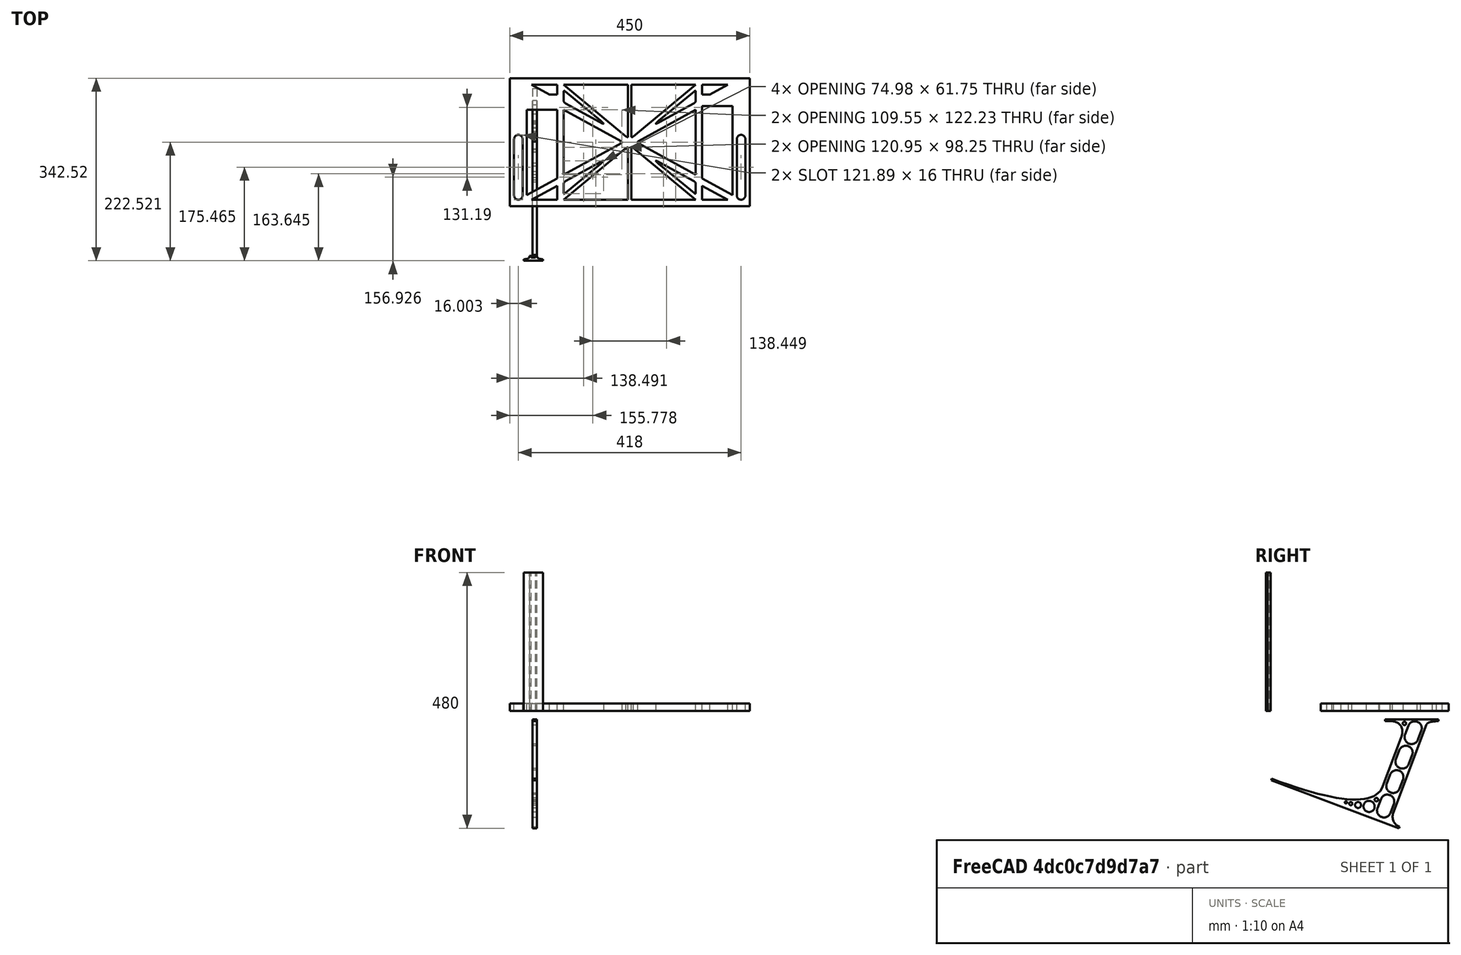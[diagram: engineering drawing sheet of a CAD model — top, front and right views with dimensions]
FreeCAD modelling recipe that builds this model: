
FCSTD DOCUMENT  (FreeCAD 0.19R0.19.2)
Label: laptopStand077
License: All rights reserved
LicenseURL: http://en.wikipedia.org/wiki/All_rights_reserved
objects: Sketcher::SketchObject×3, Part::Extrusion×3
note: 6 computed .brp shape members not serialized (recipe doc carries the construction recipe); baked Part::Feature solids carry a one-line shape summary decoded from their .brp

FEATURE [Sketcher::SketchObject] Sketch
  FullyConstrained = true
  sketch-geometry (172):
    g0: LineSegment StartX=-10.9272 StartY=-82.7794 StartZ=0 EndX=46.0728 EndY=-51.4823 EndZ=0
    g1: LineSegment StartX=366.073 StartY=-91.7794 StartZ=0 EndX=318.073 EndY=-65.424 EndZ=0
    g2: LineSegment StartX=-10.9272 StartY=77.3346 StartZ=0 EndX=-10.9272 EndY=-82.7794 EndZ=0
    g3: LineSegment StartX=375.073 StartY=-82.7794 StartZ=0 EndX=375.073 EndY=83.9235 EndZ=0
    g4: LineSegment StartX=-1.92719 StartY=-91.7794 StartZ=0 EndX=46.0728 EndY=-91.7794 EndZ=0
    g5: LineSegment StartX=318.073 StartY=124.221 StartZ=0 EndX=366.073 EndY=124.221 EndZ=0
    g6: LineSegment StartX=306.073 StartY=124.221 StartZ=0 EndX=189.124 EndY=27.0628 EndZ=0
    g7: LineSegment StartX=58.0728 StartY=-91.7794 StartZ=0 EndX=175.022 EndY=5.37834 EndZ=0
    g8: LineSegment StartX=175.022 StartY=27.0628 StartZ=0 EndX=58.0728 EndY=124.221 EndZ=0
    g9: LineSegment StartX=189.124 StartY=5.37834 StartZ=0 EndX=306.073 EndY=-91.7794 EndZ=0
    g10: LineSegment StartX=306.073 StartY=77.3346 StartZ=0 EndX=306.073 EndY=-44.8935 EndZ=0
    g11: LineSegment StartX=318.073 StartY=83.9235 StartZ=0 EndX=318.073 EndY=-51.4823 EndZ=0
    g12: LineSegment StartX=318.073 StartY=-51.4823 StartZ=0 EndX=375.073 EndY=-82.7794 EndZ=0
    g13: LineSegment StartX=318.073 StartY=-65.424 StartZ=0 EndX=318.073 EndY=-91.7794 EndZ=0
    g14: LineSegment StartX=318.073 StartY=-91.7794 StartZ=0 EndX=366.073 EndY=-91.7794 EndZ=0
    g15: LineSegment StartX=58.0728 StartY=-44.8935 StartZ=0 EndX=58.0728 EndY=77.3346 EndZ=0
    g16: LineSegment StartX=46.0728 StartY=-65.424 StartZ=0 EndX=-1.92719 EndY=-91.7794 EndZ=0
    g17: LineSegment StartX=46.0728 StartY=-65.424 StartZ=0 EndX=46.0728 EndY=-91.7794 EndZ=0
    g18: LineSegment StartX=46.0728 StartY=77.3346 StartZ=0 EndX=46.0728 EndY=-51.4823 EndZ=0
    g19: LineSegment StartX=-42.9272 StartY=136.221 StartZ=0 EndX=-42.9272 EndY=-103.779 EndZ=0
    g20: LineSegment StartX=407.073 StartY=136.221 StartZ=0 EndX=407.073 EndY=-103.779 EndZ=0
    g21: LineSegment StartX=179.022 StartY=27.0628 StartZ=0 EndX=179.022 EndY=124.221 EndZ=0
    g22: LineSegment StartX=185.124 StartY=27.0628 StartZ=0 EndX=185.124 EndY=124.221 EndZ=0
    g23: ArcOfCircle CenterX=-26.9272 CenterY=22.1087 CenterZ=0 NormalX=0 NormalY=0 NormalZ=1 AngleXU=0 Radius=8 StartAngle=1e-16 EndAngle=3.14159
    g24: ArcOfCircle CenterX=-26.9272 CenterY=-83.7794 CenterZ=0 NormalX=0 NormalY=0 NormalZ=1 AngleXU=0 Radius=8 StartAngle=3.14159 EndAngle=6.28319
    g25: LineSegment StartX=-34.9272 StartY=22.1087 StartZ=0 EndX=-34.9272 EndY=-83.7794 EndZ=0
    g26: LineSegment StartX=-18.9272 StartY=22.1087 StartZ=0 EndX=-18.9272 EndY=-83.7794 EndZ=0
    g27: LineSegment StartX=185.124 StartY=-91.7794 StartZ=0 EndX=306.073 EndY=-91.7794 EndZ=0
    g28: LineSegment StartX=179.022 StartY=-91.7794 StartZ=0 EndX=58.0728 EndY=-91.7794 EndZ=0
    g29: LineSegment StartX=306.073 StartY=124.221 StartZ=0 EndX=185.124 EndY=124.221 EndZ=0
    g30: LineSegment StartX=179.022 StartY=124.221 StartZ=0 EndX=58.0728 EndY=124.221 EndZ=0
    g31: ArcOfCircle CenterX=391.073 CenterY=22.1087 CenterZ=0 NormalX=0 NormalY=0 NormalZ=1 AngleXU=0 Radius=8 StartAngle=-4.4e-15 EndAngle=3.14159
    g32: LineSegment StartX=399.073 StartY=22.1087 StartZ=0 EndX=399.073 EndY=-83.7794 EndZ=0
    g33: LineSegment StartX=383.073 StartY=22.1087 StartZ=0 EndX=383.073 EndY=-83.7794 EndZ=0
    g34: ArcOfCircle CenterX=391.073 CenterY=-83.7794 CenterZ=0 NormalX=0 NormalY=0 NormalZ=1 AngleXU=0 Radius=8 StartAngle=3.14159 EndAngle=6.28319
    g35: Circle CenterX=175.022 CenterY=27.0628 CenterZ=0 NormalX=0 NormalY=0 NormalZ=1 AngleXU=0 Radius=1
    g36: Circle CenterX=179.022 CenterY=24.8665 CenterZ=0 NormalX=0 NormalY=0 NormalZ=1 AngleXU=0 Radius=1
    g37: Circle CenterX=179.022 CenterY=27.0628 CenterZ=0 NormalX=0 NormalY=0 NormalZ=1 AngleXU=0 Radius=1
    g38: BSplineCurve PolesCount=3 KnotsCount=2 Degree=2 IsPeriodic=0
    g39: GeomPoint X=175.022 Y=27.0628 Z=0
    g40: GeomPoint X=179.022 Y=27.0628 Z=0
    g41: Circle CenterX=189.124 CenterY=27.0628 CenterZ=0 NormalX=0 NormalY=0 NormalZ=1 AngleXU=0 Radius=1
    g42: Circle CenterX=185.124 CenterY=24.8665 CenterZ=0 NormalX=0 NormalY=0 NormalZ=1 AngleXU=0 Radius=1
    g43: Circle CenterX=185.124 CenterY=27.0628 CenterZ=0 NormalX=0 NormalY=0 NormalZ=1 AngleXU=0 Radius=1
    g44: BSplineCurve PolesCount=3 KnotsCount=2 Degree=2 IsPeriodic=0
    g45: GeomPoint X=189.124 Y=27.0628 Z=0
    g46: GeomPoint X=185.124 Y=27.0628 Z=0
    g47: Circle CenterX=175.022 CenterY=5.37834 CenterZ=0 NormalX=0 NormalY=0 NormalZ=1 AngleXU=0 Radius=1
    g48: Circle CenterX=179.022 CenterY=7.57463 CenterZ=0 NormalX=0 NormalY=0 NormalZ=1 AngleXU=0 Radius=1
    g49: Circle CenterX=179.022 CenterY=5.34704 CenterZ=0 NormalX=0 NormalY=0 NormalZ=1 AngleXU=0 Radius=1
    g50: BSplineCurve PolesCount=3 KnotsCount=2 Degree=2 IsPeriodic=0
    g51: GeomPoint X=175.022 Y=5.37834 Z=0
    g52: GeomPoint X=179.022 Y=5.34704 Z=0
    g53: Circle CenterX=189.124 CenterY=5.37834 CenterZ=0 NormalX=0 NormalY=0 NormalZ=1 AngleXU=0 Radius=1
    g54: Circle CenterX=185.124 CenterY=7.57463 CenterZ=0 NormalX=0 NormalY=0 NormalZ=1 AngleXU=0 Radius=1
    g55: Circle CenterX=185.124 CenterY=5.34704 CenterZ=0 NormalX=0 NormalY=0 NormalZ=1 AngleXU=0 Radius=1
    g56: BSplineCurve PolesCount=3 KnotsCount=2 Degree=2 IsPeriodic=0
    g57: GeomPoint X=189.124 Y=5.37834 Z=0
    g58: GeomPoint X=185.124 Y=5.34704 Z=0
    g59: LineSegment StartX=179.022 StartY=5.34704 StartZ=0 EndX=179.022 EndY=-91.7794 EndZ=0
    g60: LineSegment StartX=185.124 StartY=-91.7794 StartZ=0 EndX=185.124 EndY=5.34704 EndZ=0
    g61: Circle CenterX=165.871 CenterY=18.1458 CenterZ=0 NormalX=0 NormalY=0 NormalZ=1 AngleXU=0 Radius=1
    g62: Circle CenterX=169.377 CenterY=16.2206 CenterZ=0 NormalX=0 NormalY=0 NormalZ=1 AngleXU=0 Radius=1
    g63: Circle CenterX=165.871 CenterY=14.2954 CenterZ=0 NormalX=0 NormalY=0 NormalZ=1 AngleXU=0 Radius=1
    g64: BSplineCurve PolesCount=3 KnotsCount=2 Degree=2 IsPeriodic=0
    g65: GeomPoint X=165.871 Y=18.1458 Z=0
    g66: GeomPoint X=165.871 Y=14.2954 Z=0
    g67: Circle CenterX=198.275 CenterY=18.1458 CenterZ=0 NormalX=0 NormalY=0 NormalZ=1 AngleXU=0 Radius=1
    g68: Circle CenterX=194.768 CenterY=16.2206 CenterZ=0 NormalX=0 NormalY=0 NormalZ=1 AngleXU=0 Radius=1
    g69: Circle CenterX=198.275 CenterY=14.2954 CenterZ=0 NormalX=0 NormalY=0 NormalZ=1 AngleXU=0 Radius=1
    g70: BSplineCurve PolesCount=3 KnotsCount=2 Degree=2 IsPeriodic=0
    g71: GeomPoint X=198.275 Y=18.1458 Z=0
    g72: GeomPoint X=198.275 Y=14.2954 Z=0
    g73: LineSegment StartX=165.871 StartY=18.1458 StartZ=0 EndX=58.0728 EndY=77.3346 EndZ=0
    g74: LineSegment StartX=58.0728 StartY=-44.8935 StartZ=0 EndX=165.871 EndY=14.2954 EndZ=0
    g75: LineSegment StartX=198.275 StartY=18.1458 StartZ=0 EndX=306.073 EndY=77.3346 EndZ=0
    g76: LineSegment StartX=198.275 StartY=14.2954 StartZ=0 EndX=306.073 EndY=-44.8935 EndZ=0
    g77: LineSegment StartX=407.073 StartY=-103.779 StartZ=0 EndX=-42.9272 EndY=-103.779 EndZ=0
    g78: LineSegment StartX=407.073 StartY=136.221 StartZ=0 EndX=-42.9272 EndY=136.221 EndZ=0
    g79: LineSegment StartX=46.0728 StartY=77.3346 StartZ=0 EndX=-10.9272 EndY=77.3346 EndZ=0
    g80: LineSegment StartX=46.0728 StartY=105.865 StartZ=0 EndX=31.5028 EndY=105.865 EndZ=0
    g81: LineSegment StartX=46.0728 StartY=124.221 StartZ=0 EndX=46.0728 EndY=105.865 EndZ=0
    g82: LineSegment StartX=-1.92719 StartY=124.221 StartZ=0 EndX=31.5028 EndY=105.865 EndZ=0
    g83: LineSegment StartX=46.0728 StartY=124.221 StartZ=0 EndX=-1.92719 EndY=124.221 EndZ=0
    g84: LineSegment StartX=318.073 StartY=83.9235 StartZ=0 EndX=375.073 EndY=83.9235 EndZ=0
    g85: LineSegment StartX=318.073 StartY=105.865 StartZ=0 EndX=332.643 EndY=105.865 EndZ=0
    g86: LineSegment StartX=332.643 StartY=105.865 StartZ=0 EndX=366.073 EndY=124.221 EndZ=0
    g87: LineSegment StartX=318.073 StartY=124.221 StartZ=0 EndX=318.073 EndY=105.865 EndZ=0
    g88: Circle CenterX=125.607 CenterY=54.1951 CenterZ=0 NormalX=0 NormalY=0 NormalZ=1 AngleXU=0 Radius=1
    g89: Circle CenterX=139.632 CenterY=46.4944 CenterZ=0 NormalX=0 NormalY=0 NormalZ=1 AngleXU=0 Radius=1
    g90: Circle CenterX=127.326 CenterY=56.7187 CenterZ=0 NormalX=0 NormalY=0 NormalZ=1 AngleXU=0 Radius=1
    g91: BSplineCurve PolesCount=3 KnotsCount=2 Degree=2 IsPeriodic=0
    g92: GeomPoint X=125.607 Y=54.1951 Z=0
    g93: GeomPoint X=127.326 Y=56.7187 Z=0
    g94: Circle CenterX=236.821 CenterY=56.7187 CenterZ=0 NormalX=0 NormalY=0 NormalZ=1 AngleXU=0 Radius=1
    g95: Circle CenterX=224.513 CenterY=46.4944 CenterZ=0 NormalX=0 NormalY=0 NormalZ=1 AngleXU=0 Radius=1
    g96: Circle CenterX=238.538 CenterY=54.1951 CenterZ=0 NormalX=0 NormalY=0 NormalZ=1 AngleXU=0 Radius=1
    g97: BSplineCurve PolesCount=3 KnotsCount=2 Degree=2 IsPeriodic=0
    g98: GeomPoint X=236.821 Y=56.7187 Z=0
    g99: GeomPoint X=238.538 Y=54.1951 Z=0
    g100: Circle CenterX=238.538 CenterY=-21.7539 CenterZ=0 NormalX=0 NormalY=0 NormalZ=1 AngleXU=0 Radius=1
    g101: Circle CenterX=224.513 CenterY=-14.0532 CenterZ=0 NormalX=0 NormalY=0 NormalZ=1 AngleXU=0 Radius=1
    g102: Circle CenterX=236.821 CenterY=-24.2775 CenterZ=0 NormalX=0 NormalY=0 NormalZ=1 AngleXU=0 Radius=1
    g103: BSplineCurve PolesCount=3 KnotsCount=2 Degree=2 IsPeriodic=0
    g104: GeomPoint X=238.538 Y=-21.7539 Z=0
    g105: GeomPoint X=236.821 Y=-24.2775 Z=0
    g106: Circle CenterX=125.607 CenterY=-21.7539 CenterZ=0 NormalX=0 NormalY=0 NormalZ=1 AngleXU=0 Radius=1
    g107: Circle CenterX=139.632 CenterY=-14.0532 CenterZ=0 NormalX=0 NormalY=0 NormalZ=1 AngleXU=0 Radius=1
    g108: Circle CenterX=127.325 CenterY=-24.2775 CenterZ=0 NormalX=0 NormalY=0 NormalZ=1 AngleXU=0 Radius=1
    g109: BSplineCurve PolesCount=3 KnotsCount=2 Degree=2 IsPeriodic=0
    g110: GeomPoint X=125.607 Y=-21.7539 Z=0
    g111: GeomPoint X=127.325 Y=-24.2775 Z=0
    g112: Circle CenterX=302.996 CenterY=111.695 CenterZ=0 NormalX=0 NormalY=0 NormalZ=1 AngleXU=0 Radius=1
    g113: Circle CenterX=306.073 CenterY=114.251 CenterZ=0 NormalX=0 NormalY=0 NormalZ=1 AngleXU=0 Radius=1
    g114: Circle CenterX=306.073 CenterY=110.251 CenterZ=0 NormalX=0 NormalY=0 NormalZ=1 AngleXU=0 Radius=1
    g115: BSplineCurve PolesCount=3 KnotsCount=2 Degree=2 IsPeriodic=0
    g116: GeomPoint X=302.996 Y=111.695 Z=0
    g117: GeomPoint X=306.073 Y=110.251 Z=0
    g118: Circle CenterX=306.073 CenterY=95.2763 CenterZ=0 NormalX=0 NormalY=0 NormalZ=1 AngleXU=0 Radius=1
    g119: Circle CenterX=306.073 CenterY=91.2763 CenterZ=0 NormalX=0 NormalY=0 NormalZ=1 AngleXU=0 Radius=1
    g120: Circle CenterX=302.567 CenterY=89.3511 CenterZ=0 NormalX=0 NormalY=0 NormalZ=1 AngleXU=0 Radius=1
    g121: BSplineCurve PolesCount=3 KnotsCount=2 Degree=2 IsPeriodic=0
    g122: GeomPoint X=306.073 Y=95.2763 Z=0
    g123: GeomPoint X=302.567 Y=89.3511 Z=0
    g124: LineSegment StartX=306.073 StartY=110.251 StartZ=0 EndX=306.073 EndY=95.2763 EndZ=0
    g125: LineSegment StartX=302.996 StartY=111.695 StartZ=0 EndX=236.821 EndY=56.7187 EndZ=0
    g126: LineSegment StartX=238.538 StartY=54.1951 StartZ=0 EndX=302.567 EndY=89.3511 EndZ=0
    g127: Circle CenterX=61.1496 CenterY=111.695 CenterZ=0 NormalX=0 NormalY=0 NormalZ=1 AngleXU=0 Radius=1
    g128: Circle CenterX=58.0728 CenterY=114.251 CenterZ=0 NormalX=0 NormalY=0 NormalZ=1 AngleXU=0 Radius=1
    g129: Circle CenterX=58.0728 CenterY=110.251 CenterZ=0 NormalX=0 NormalY=0 NormalZ=1 AngleXU=0 Radius=1
    g130: BSplineCurve PolesCount=3 KnotsCount=2 Degree=2 IsPeriodic=0
    g131: GeomPoint X=61.1496 Y=111.695 Z=0
    g132: GeomPoint X=58.0728 Y=110.251 Z=0
    g133: Circle CenterX=61.5791 CenterY=89.3511 CenterZ=0 NormalX=0 NormalY=0 NormalZ=1 AngleXU=0 Radius=1
    g134: Circle CenterX=58.0728 CenterY=91.2763 CenterZ=0 NormalX=0 NormalY=0 NormalZ=1 AngleXU=0 Radius=1
    g135: Circle CenterX=58.0728 CenterY=95.2763 CenterZ=0 NormalX=0 NormalY=0 NormalZ=1 AngleXU=0 Radius=1
    g136: BSplineCurve PolesCount=3 KnotsCount=2 Degree=2 IsPeriodic=0
    g137: GeomPoint X=61.5791 Y=89.3511 Z=0
    g138: GeomPoint X=58.0728 Y=95.2763 Z=0
    g139: LineSegment StartX=58.0728 StartY=110.251 StartZ=0 EndX=58.0728 EndY=95.2763 EndZ=0
    g140: LineSegment StartX=61.1496 StartY=111.695 StartZ=0 EndX=127.326 EndY=56.7187 EndZ=0
    g141: LineSegment StartX=125.607 StartY=54.1951 StartZ=0 EndX=61.5791 EndY=89.3511 EndZ=0
    g142: Circle CenterX=61.5791 CenterY=-56.9099 CenterZ=0 NormalX=0 NormalY=0 NormalZ=1 AngleXU=0 Radius=1
    g143: Circle CenterX=58.0728 CenterY=-58.8351 CenterZ=0 NormalX=0 NormalY=0 NormalZ=1 AngleXU=0 Radius=1
    g144: Circle CenterX=58.0728 CenterY=-62.8351 CenterZ=0 NormalX=0 NormalY=0 NormalZ=1 AngleXU=0 Radius=1
    g145: BSplineCurve PolesCount=3 KnotsCount=2 Degree=2 IsPeriodic=0
    g146: GeomPoint X=61.5791 Y=-56.9099 Z=0
    g147: GeomPoint X=58.0728 Y=-62.8351 Z=0
    g148: Circle CenterX=58.0728 CenterY=-77.8102 CenterZ=0 NormalX=0 NormalY=0 NormalZ=1 AngleXU=0 Radius=1
    g149: Circle CenterX=58.0728 CenterY=-81.8102 CenterZ=0 NormalX=0 NormalY=0 NormalZ=1 AngleXU=0 Radius=1
    g150: Circle CenterX=61.1496 CenterY=-79.2541 CenterZ=0 NormalX=0 NormalY=0 NormalZ=1 AngleXU=0 Radius=1
    g151: BSplineCurve PolesCount=3 KnotsCount=2 Degree=2 IsPeriodic=0
    g152: GeomPoint X=58.0728 Y=-77.8102 Z=0
    g153: GeomPoint X=61.1496 Y=-79.2541 Z=0
    g154: LineSegment StartX=58.0728 StartY=-62.8351 StartZ=0 EndX=58.0728 EndY=-77.8102 EndZ=0
    g155: LineSegment StartX=61.1496 StartY=-79.2541 StartZ=0 EndX=127.325 EndY=-24.2775 EndZ=0
    g156: LineSegment StartX=125.607 StartY=-21.7539 StartZ=0 EndX=61.5791 EndY=-56.9099 EndZ=0
    g157: Circle CenterX=302.567 CenterY=-56.9099 CenterZ=0 NormalX=0 NormalY=0 NormalZ=1 AngleXU=0 Radius=1
    g158: Circle CenterX=306.073 CenterY=-58.8351 CenterZ=0 NormalX=0 NormalY=0 NormalZ=1 AngleXU=0 Radius=1
    g159: Circle CenterX=306.073 CenterY=-62.8351 CenterZ=0 NormalX=0 NormalY=0 NormalZ=1 AngleXU=0 Radius=1
    g160: BSplineCurve PolesCount=3 KnotsCount=2 Degree=2 IsPeriodic=0
    g161: GeomPoint X=302.567 Y=-56.9099 Z=0
    g162: GeomPoint X=306.073 Y=-62.8351 Z=0
    g163: Circle CenterX=302.996 CenterY=-79.2541 CenterZ=0 NormalX=0 NormalY=0 NormalZ=1 AngleXU=0 Radius=1
    g164: Circle CenterX=306.073 CenterY=-81.8102 CenterZ=0 NormalX=0 NormalY=0 NormalZ=1 AngleXU=0 Radius=1
    g165: Circle CenterX=306.073 CenterY=-77.8102 CenterZ=0 NormalX=0 NormalY=0 NormalZ=1 AngleXU=0 Radius=1
    g166: BSplineCurve PolesCount=3 KnotsCount=2 Degree=2 IsPeriodic=0
    g167: GeomPoint X=302.996 Y=-79.2541 Z=0
    g168: GeomPoint X=306.073 Y=-77.8102 Z=0
    g169: LineSegment StartX=306.073 StartY=-62.8351 StartZ=0 EndX=306.073 EndY=-77.8102 EndZ=0
    g170: LineSegment StartX=302.996 StartY=-79.2541 StartZ=0 EndX=236.821 EndY=-24.2775 EndZ=0
    g171: LineSegment StartX=238.538 StartY=-21.7539 StartZ=0 EndX=302.567 EndY=-56.9099 EndZ=0
  constraints (300):
    c: Horizontal(g4)
    c: Horizontal(g5)
    c: Coincident(g11,g12)
    c: Coincident(g13,g1)
    c: Tangent(g11,g13)
    c: Coincident(g17,g16)
    c: Coincident(g0,g18)
    c: Block(g8)
    c: Block(g6)
    c: Block(g12)
    c: Block(g3)
    c: Block(g1)
    c: Block(g13)
    c: Block(g9)
    c: Block(g7)
    c: Block(g17)
    c: Block(g16)
    c: Block(g0)
    c: Block(g2)
    c: Block(g10)
    c: Block(g5)
    c: Block(g14)
    c: Block(g4)
    c: Vertical(g19)
    c: Vertical(g20)
    c: Block(g20)
    c: Block(g19)
    c: Vertical(g21)
    c: Vertical(g22)
    c: Block(g21)
    c: Block(g22)
    c: Tangent(g23,g26) = 1.5708
    c: Tangent(g23,g25) = -1.5708
    c: Tangent(g25,g24) = -1.5708
    c: Tangent(g26,g24) = 1.5708
    c: Vertical(g25)
    c: Equal(g23,g24)
    c: Block(g26)
    c: Block(g25)
    c: Coincident(g27,g9)
    c: Horizontal(g27)
    c: Coincident(g28,g7)
    c: Horizontal(g28)
    c: Coincident(g29,g6)
    c: Coincident(g29,g22)
    c: Horizontal(g29)
    c: Coincident(g30,g21)
    c: Coincident(g30,g8)
    c: Horizontal(g30)
    c: Tangent(g31,g32) = 1.5708
    c: Tangent(g32,g34) = 1.5708
    c: Equal(g31,g34)
    c: Coincident(g33,g31)
    c: Coincident(g33,g34)
    c: Block(g32)
    c: Block(g33)
    c: Coincident(g38,g8)
    c: Weight(g35) = 1
    c: Equal(g35,g36)
    c: Equal(g35,g37)
    c: Coincident(g38,g21)
    c: InternalAlignment(g35,g38)
    c: InternalAlignment(g36,g38)
    c: InternalAlignment(g37,g38)
    c: InternalAlignment(g39,g38)
    c: InternalAlignment(g40,g38)
    c: Coincident(g44,g6)
    c: Weight(g41) = 1
    c: Equal(g41,g42)
    c: Equal(g41,g43)
    c: Coincident(g44,g22)
    c: InternalAlignment(g41,g44)
    c: InternalAlignment(g42,g44)
    c: InternalAlignment(g43,g44)
    c: InternalAlignment(g45,g44)
    c: InternalAlignment(g46,g44)
    c: Block(g44)
    c: Block(g38)
    c: Coincident(g50,g7)
    c: Weight(g47) = 1
    c: Equal(g47,g48)
    c: Equal(g47,g49)
    c: InternalAlignment(g47,g50)
    c: InternalAlignment(g48,g50)
    c: InternalAlignment(g49,g50)
    c: InternalAlignment(g51,g50)
    c: InternalAlignment(g52,g50)
    c: Weight(g53) = 1
    c: Equal(g53,g54)
    c: Equal(g53,g55)
    c: InternalAlignment(g53,g56)
    c: InternalAlignment(g54,g56)
    c: InternalAlignment(g55,g56)
    c: InternalAlignment(g57,g56)
    c: InternalAlignment(g58,g56)
    c: Block(g56)
    c: Block(g50)
    c: Coincident(g59,g50)
    c: Coincident(g59,g28)
    c: Vertical(g59)
    c: Coincident(g60,g27)
    c: Coincident(g60,g56)
    c: Vertical(g60)
    c: Weight(g61) = 1
    c: Equal(g61,g62)
    c: Equal(g61,g63)
    c: InternalAlignment(g61,g64)
    c: InternalAlignment(g62,g64)
    c: InternalAlignment(g63,g64)
    c: InternalAlignment(g65,g64)
    c: InternalAlignment(g66,g64)
    c: Weight(g67) = 1
    c: Equal(g67,g68)
    c: Equal(g67,g69)
    c: InternalAlignment(g67,g70)
    c: InternalAlignment(g68,g70)
    c: InternalAlignment(g69,g70)
    c: InternalAlignment(g71,g70)
    c: InternalAlignment(g72,g70)
    c: Block(g64)
    c: Block(g70)
    c: Coincident(g73,g64)
    c: Coincident(g73,g15)
    c: Coincident(g74,g15)
    c: Coincident(g74,g64)
    c: Coincident(g75,g70)
    c: Coincident(g75,g10)
    c: Coincident(g76,g70)
    c: Coincident(g76,g10)
    c: Block(g15)
    c: Coincident(g77,g20)
    c: Coincident(g77,g19)
    c: Horizontal(g77)
    c: Distance(g77) = 450
    c: Coincident(g78,g20)
    c: Coincident(g78,g19)
    c: Horizontal(g78)
    c: Horizontal(g79)
    c: Coincident(g18,g79)
    c: Horizontal(g80)
    c: Vertical(g81)
    c: Block(g81)
    c: Block(g80)
    c: Block(g79)
    c: Distance(g81) = 18.3554
    c: Coincident(g83,g81)
    c: Coincident(g83,g82)
    c: Horizontal(g83)
    c: Block(g83)
    c: Block(g82)
    c: Coincident(g80,g82)
    c: Coincident(g2,g79)
    c: Coincident(g84,g11)
    c: Horizontal(g84)
    c: Horizontal(g85)
    c: Block(g84)
    c: Coincident(g86,g5)
    c: Coincident(g87,g5)
    c: Coincident(g87,g85)
    c: Vertical(g87)
    c: Block(g87)
    c: Coincident(g85,g86)
    c: Block(g86)
    c: Coincident(g3,g84)
    c: Weight(g88) = 1
    c: Equal(g88,g89)
    c: Equal(g88,g90)
    c: InternalAlignment(g88,g91)
    c: InternalAlignment(g89,g91)
    c: InternalAlignment(g90,g91)
    c: InternalAlignment(g92,g91)
    c: InternalAlignment(g93,g91)
    c: Block(g91)
    c: Weight(g94) = 1
    c: Equal(g94,g95)
    c: Equal(g94,g96)
    c: InternalAlignment(g94,g97)
    c: InternalAlignment(g95,g97)
    c: InternalAlignment(g96,g97)
    c: InternalAlignment(g98,g97)
    c: InternalAlignment(g99,g97)
    c: Block(g97)
    c: Weight(g100) = 1
    c: Equal(g100,g101)
    c: Equal(g100,g102)
    c: InternalAlignment(g100,g103)
    c: InternalAlignment(g101,g103)
    c: InternalAlignment(g102,g103)
    c: InternalAlignment(g104,g103)
    c: InternalAlignment(g105,g103)
    c: Block(g103)
    c: Weight(g106) = 1
    c: Equal(g106,g107)
    c: Equal(g106,g108)
    c: InternalAlignment(g106,g109)
    c: InternalAlignment(g107,g109)
    c: InternalAlignment(g108,g109)
    c: InternalAlignment(g110,g109)
    c: InternalAlignment(g111,g109)
    c: Block(g109)
    c: Weight(g112) = 1
    c: Equal(g112,g113)
    c: Equal(g112,g114)
    c: InternalAlignment(g112,g115)
    c: InternalAlignment(g113,g115)
    c: InternalAlignment(g114,g115)
    c: InternalAlignment(g116,g115)
    c: InternalAlignment(g117,g115)
    c: Weight(g118) = 1
    c: Equal(g118,g119)
    c: Equal(g118,g120)
    c: InternalAlignment(g118,g121)
    c: InternalAlignment(g119,g121)
    c: InternalAlignment(g120,g121)
    c: InternalAlignment(g122,g121)
    c: InternalAlignment(g123,g121)
    c: Block(g115)
    c: Block(g121)
    c: Coincident(g124,g115)
    c: Coincident(g124,g121)
    c: Vertical(g124)
    c: Coincident(g125,g115)
    c: Coincident(g125,g97)
    c: Coincident(g126,g97)
    c: Coincident(g126,g121)
    c: Weight(g127) = 1
    c: Equal(g127,g128)
    c: Equal(g127,g129)
    c: InternalAlignment(g127,g130)
    c: InternalAlignment(g128,g130)
    c: InternalAlignment(g129,g130)
    c: InternalAlignment(g131,g130)
    c: InternalAlignment(g132,g130)
    c: Weight(g133) = 1
    c: Equal(g133,g134)
    c: Equal(g133,g135)
    c: InternalAlignment(g133,g136)
    c: InternalAlignment(g134,g136)
    c: InternalAlignment(g135,g136)
    c: InternalAlignment(g137,g136)
    c: InternalAlignment(g138,g136)
    c: Block(g130)
    c: Block(g136)
    c: Coincident(g139,g130)
    c: Coincident(g139,g136)
    c: Vertical(g139)
    c: Coincident(g140,g130)
    c: Coincident(g140,g91)
    c: Coincident(g141,g91)
    c: Coincident(g141,g136)
    c: Weight(g142) = 1
    c: Equal(g142,g143)
    c: Equal(g142,g144)
    c: InternalAlignment(g142,g145)
    c: InternalAlignment(g143,g145)
    c: InternalAlignment(g144,g145)
    c: InternalAlignment(g146,g145)
    c: InternalAlignment(g147,g145)
    c: Weight(g148) = 1
    c: Equal(g148,g149)
    c: Equal(g148,g150)
    c: InternalAlignment(g148,g151)
    c: InternalAlignment(g149,g151)
    c: InternalAlignment(g150,g151)
    c: InternalAlignment(g152,g151)
    c: InternalAlignment(g153,g151)
    c: Block(g145)
    c: Block(g151)
    c: Coincident(g154,g145)
    c: Coincident(g154,g151)
    c: Vertical(g154)
    c: Coincident(g155,g151)
    c: Coincident(g155,g109)
    c: Coincident(g156,g109)
    c: Coincident(g156,g145)
    c: Weight(g157) = 1
    c: Equal(g157,g158)
    c: Equal(g157,g159)
    c: InternalAlignment(g157,g160)
    c: InternalAlignment(g158,g160)
    c: InternalAlignment(g159,g160)
    c: InternalAlignment(g161,g160)
    c: InternalAlignment(g162,g160)
    c: Weight(g163) = 1
    c: Equal(g163,g164)
    c: Equal(g163,g165)
    c: InternalAlignment(g163,g166)
    c: InternalAlignment(g164,g166)
    c: InternalAlignment(g165,g166)
    c: InternalAlignment(g167,g166)
    c: InternalAlignment(g168,g166)
    c: Block(g160)
    c: Block(g166)
    c: Coincident(g169,g160)
    c: Coincident(g169,g166)
    c: Vertical(g169)
    c: Coincident(g170,g166)
    c: Coincident(g170,g103)
    c: Coincident(g171,g103)
    c: Coincident(g171,g160)
FEATURE [Sketcher::SketchObject] Sketch001
  FullyConstrained = true
  MapMode = 4
  Placement = pos=(0,0,0) rot=(0.57735,0.57735,0.57735;2.0944rad)
  Support = -> [Sketch]
  sketch-geometry (46):
    g0: BSplineCurve PolesCount=3 KnotsCount=2 Degree=2 IsPeriodic=0
    g1: ArcOfCircle CenterX=73.1223 CenterY=-32.291 CenterZ=0 NormalX=0 NormalY=0 NormalZ=1 AngleXU=0 Radius=13 StartAngle=5.92268 EndAngle=9.06428
    g2: ArcOfCircle CenterX=66.7816 CenterY=-49.1439 CenterZ=0 NormalX=0 NormalY=0 NormalZ=1 AngleXU=0 Radius=13 StartAngle=2.78068 EndAngle=5.92131
    g3: ArcOfCircle CenterX=55.9263 CenterY=-78.1807 CenterZ=0 NormalX=0 NormalY=0 NormalZ=1 AngleXU=0 Radius=13 StartAngle=5.92268 EndAngle=9.06428
    g4: ArcOfCircle CenterX=49.5884 CenterY=-95.0342 CenterZ=0 NormalX=0 NormalY=0 NormalZ=1 AngleXU=0 Radius=13 StartAngle=2.78068 EndAngle=5.92131
    g5: ArcOfCircle CenterX=38.7206 CenterY=-124.067 CenterZ=0 NormalX=0 NormalY=0 NormalZ=1 AngleXU=0 Radius=13 StartAngle=5.92268 EndAngle=9.06428
    g6: ArcOfCircle CenterX=32.3875 CenterY=-140.92 CenterZ=0 NormalX=0 NormalY=0 NormalZ=1 AngleXU=0 Radius=13 StartAngle=2.78068 EndAngle=5.92131
    g7: ArcOfCircle CenterX=21.4715 CenterY=-169.934 CenterZ=0 NormalX=0 NormalY=0 NormalZ=1 AngleXU=0 Radius=13 StartAngle=5.92268 EndAngle=9.06428
    g8: ArcOfCircle CenterX=15.1336 CenterY=-186.787 CenterZ=0 NormalX=0 NormalY=0 NormalZ=1 AngleXU=0 Radius=13 StartAngle=2.78068 EndAngle=5.92131
    g9-g12: Circle x4 (B-spline internal-alignment scaffolding for g13; pole/knot coordinates omitted)
    g13: BSplineCurve PolesCount=4 KnotsCount=2 Degree=3 IsPeriodic=0
    g14: GeomPoint X=28.8094 Y=-19.0875 Z=0
    g15: GeomPoint X=47.0443 Y=-50.4712 Z=0
    g16: Circle CenterX=53.5586 CenterY=-23.2695 CenterZ=0 NormalX=0 NormalY=0 NormalZ=1 AngleXU=0 Radius=3.24518
    g17: Circle CenterX=-195.441 CenterY=-127.082 CenterZ=0 NormalX=0 NormalY=0 NormalZ=1 AngleXU=0 Radius=1
    g18: Circle CenterX=-8.24091 CenterY=-197.481 CenterZ=0 NormalX=0 NormalY=0 NormalZ=1 AngleXU=0 Radius=1
    g19: Circle CenterX=12.8789 CenterY=-141.321 CenterZ=0 NormalX=0 NormalY=0 NormalZ=1 AngleXU=0 Radius=1
    g20: BSplineCurve PolesCount=3 KnotsCount=2 Degree=2 IsPeriodic=0
    g21: GeomPoint X=-195.441 Y=-127.082 Z=0
    g22: GeomPoint X=12.8789 Y=-141.321 Z=0
    g23: Circle CenterX=-12.8016 CenterY=-179.036 CenterZ=0 NormalX=0 NormalY=0 NormalZ=1 AngleXU=0 Radius=10.5072
    g24: Circle CenterX=0.933922 CenterY=-166.43 CenterZ=0 NormalX=0 NormalY=0 NormalZ=1 AngleXU=0 Radius=3.26661
    g25: Circle CenterX=-33.5518 CenterY=-176.44 CenterZ=0 NormalX=0 NormalY=0 NormalZ=1 AngleXU=0 Radius=5.64388
    g26: Circle CenterX=-47.2366 CenterY=-173.859 CenterZ=0 NormalX=0 NormalY=0 NormalZ=1 AngleXU=0 Radius=3.01653
    g27: Circle CenterX=-56.2595 CenterY=-171.456 CenterZ=0 NormalX=0 NormalY=0 NormalZ=1 AngleXU=0 Radius=2.12826
    g28: ArcOfCircle CenterX=51.2151 CenterY=-198.473 CenterZ=0 NormalX=0 NormalY=0 NormalZ=1 AngleXU=0 Radius=20 StartAngle=2.78189 EndAngle=4.35269
    g29: LineSegment StartX=32.4951 StartY=-191.433 StartZ=0 EndX=94.6578 EndY=-26.1352 EndZ=0
    g30: LineSegment StartX=43.1192 StartY=-220.001 StartZ=0 EndX=-196.497 EndY=-129.89 EndZ=0
    g31: LineSegment StartX=43.1192 StartY=-220.001 StartZ=0 EndX=44.1752 EndY=-217.193 EndZ=0
    g32: LineSegment StartX=117.223 StartY=-19.0875 StartZ=0 EndX=117.223 EndY=-16.0875 EndZ=0
    g33: LineSegment StartX=117.223 StartY=-16.0875 StartZ=0 EndX=17.2232 EndY=-16.0875 EndZ=0
    g34: LineSegment StartX=17.2232 StartY=-16.0875 StartZ=0 EndX=17.2232 EndY=-19.0875 EndZ=0
    g35: LineSegment StartX=28.8094 StartY=-19.0875 StartZ=0 EndX=17.2232 EndY=-19.0875 EndZ=0
    g36: LineSegment StartX=47.0443 StartY=-50.4712 StartZ=0 EndX=12.8789 EndY=-141.321 EndZ=0
    g37: LineSegment StartX=-195.441 StartY=-127.082 StartZ=0 EndX=-196.497 EndY=-129.89 EndZ=0
    g38: LineSegment StartX=85.2866 StartY=-36.8766 StartZ=0 EndX=78.9396 EndY=-53.7463 EndZ=0
    g39: LineSegment StartX=60.9579 StartY=-27.7053 StartZ=0 EndX=54.6191 EndY=-44.5532 EndZ=0
    g40: LineSegment StartX=68.0907 StartY=-82.7664 StartZ=0 EndX=61.7465 EndY=-99.6365 EndZ=0
    g41: LineSegment StartX=43.7619 StartY=-73.595 StartZ=0 EndX=37.426 EndY=-90.4435 EndZ=0
    g42: LineSegment StartX=50.885 StartY=-128.652 StartZ=0 EndX=44.5456 EndY=-145.522 EndZ=0
    g43: LineSegment StartX=26.5562 StartY=-119.481 StartZ=0 EndX=20.2251 EndY=-136.329 EndZ=0
    g44: LineSegment StartX=9.3071 StartY=-165.349 StartZ=0 EndX=2.97115 EndY=-182.197 EndZ=0
    g45: LineSegment StartX=33.6358 StartY=-174.52 StartZ=0 EndX=27.2917 EndY=-191.39 EndZ=0
  constraints (71):
    c: Block(g0)
    c: Block(g1)
    c: Block(g2)
    c: Block(g4)
    c: Block(g3)
    c: Block(g6)
    c: Block(g5)
    c: Block(g8)
    c: Block(g7)
    c: Weight(g9) = 1
    c: Equal(g9,g10)
    c: Equal(g9,g11)
    c: Equal(g9,g12)
    c: InternalAlignment(g9-g12 -> g13) x4
    c: InternalAlignment(g14,g13)
    c: InternalAlignment(g15,g13)
    c: Block(g16)
    c: Weight(g17) = 1
    c: Equal(g17,g18)
    c: Equal(g17,g19)
    c: InternalAlignment(g17,g20)
    c: InternalAlignment(g18,g20)
    c: InternalAlignment(g19,g20)
    c: InternalAlignment(g21,g20)
    c: InternalAlignment(g22,g20)
    c: Block(g20)
    c: Block(g23)
    c: Block(g24)
    c: Block(g25)
    c: Block(g26)
    c: Block(g27)
    c: Block(g28)
    c: Coincident(g29,g28)
    c: Coincident(g29,g0)
    c: Block(g13)
    c: Coincident(g31,g30)
    c: Coincident(g31,g28)
    c: Block(g31)
    c: Coincident(g32,g0)
    c: Vertical(g32)
    c: Coincident(g33,g32)
    c: Horizontal(g33)
    c: Coincident(g34,g33)
    c: Vertical(g34)
    c: Block(g33)
    c: Coincident(g35,g13)
    c: Coincident(g35,g34)
    c: Horizontal(g35)
    c: Coincident(g36,g13)
    c: Coincident(g36,g20)
    c: Coincident(g37,g20)
    c: Coincident(g37,g30)
    c: Block(g30)
    c: Coincident(g38,g1)
    c: Coincident(g38,g2)
    c: Coincident(g39,g1)
    c: Coincident(g39,g2)
    c: Coincident(g40,g3)
    c: Coincident(g40,g4)
    c: Coincident(g41,g3)
    c: Coincident(g41,g4)
    c: Coincident(g42,g5)
    c: Coincident(g42,g6)
    c: Coincident(g43,g5)
    c: Coincident(g43,g6)
    c: Coincident(g44,g7)
    c: Coincident(g44,g8)
    c: Coincident(g45,g7)
    c: Coincident(g45,g8)
    c: Distance(g30) = 256
    c: Distance(g33) = 100
FEATURE [Part::Extrusion] Extrude002
  Base = -> Sketch001
  Dir = (1,0,0)
  DirMode = 2
  FaceMakerClass = Part::FaceMakerBullseye
  LengthFwd = 8
  LengthRev = 0
  Solid = true
  Symmetric = false
FEATURE [Sketcher::SketchObject] Sketch002
  FullyConstrained = true
  sketch-geometry (20):
    g0: LineSegment StartX=-2.77179 StartY=-200.304 StartZ=0 EndX=5.22821 EndY=-200.304 EndZ=0
    g1: LineSegment StartX=5.22821 StartY=-200.304 StartZ=0 EndX=5.22821 EndY=-197.304 EndZ=0
    g2: LineSegment StartX=-2.77179 StartY=-200.304 StartZ=0 EndX=-2.77179 EndY=-197.304 EndZ=0
    g3: LineSegment StartX=5.22821 StartY=-197.304 StartZ=0 EndX=8.22821 EndY=-197.304 EndZ=0
    g4: LineSegment StartX=-2.77179 StartY=-197.304 StartZ=0 EndX=-5.77179 EndY=-197.304 EndZ=0
    g5: LineSegment StartX=19.2282 StartY=-203.304 StartZ=0 EndX=19.2282 EndY=-206.304 EndZ=0
    g6: LineSegment StartX=-16.7718 StartY=-203.304 StartZ=0 EndX=-16.7718 EndY=-206.304 EndZ=0
    g7: LineSegment StartX=-16.7718 StartY=-206.304 StartZ=0 EndX=19.2282 EndY=-206.304 EndZ=0
    g8: Circle CenterX=-16.7718 CenterY=-203.304 CenterZ=0 NormalX=0 NormalY=0 NormalZ=1 AngleXU=0 Radius=1
    g9: Circle CenterX=-5.77179 CenterY=-203.304 CenterZ=0 NormalX=0 NormalY=0 NormalZ=1 AngleXU=0 Radius=1
    g10: Circle CenterX=-5.77179 CenterY=-197.304 CenterZ=0 NormalX=0 NormalY=0 NormalZ=1 AngleXU=0 Radius=1
    g11: BSplineCurve PolesCount=3 KnotsCount=2 Degree=2 IsPeriodic=0
    g12: GeomPoint X=-16.7718 Y=-203.304 Z=0
    g13: GeomPoint X=-5.77179 Y=-197.304 Z=0
    g14: Circle CenterX=19.2282 CenterY=-203.304 CenterZ=0 NormalX=0 NormalY=0 NormalZ=1 AngleXU=0 Radius=1
    g15: Circle CenterX=8.22821 CenterY=-203.304 CenterZ=0 NormalX=0 NormalY=0 NormalZ=1 AngleXU=0 Radius=1
    g16: Circle CenterX=8.22821 CenterY=-197.304 CenterZ=0 NormalX=0 NormalY=0 NormalZ=1 AngleXU=0 Radius=1
    g17: BSplineCurve PolesCount=3 KnotsCount=2 Degree=2 IsPeriodic=0
    g18: GeomPoint X=19.2282 Y=-203.304 Z=0
    g19: GeomPoint X=8.22821 Y=-197.304 Z=0
  constraints (41):
    c: Horizontal(g0)
    c: Distance(g0) = 8
    c: Coincident(g1,g0)
    c: Vertical(g1)
    c: Distance(g1) = 3
    c: Coincident(g2,g0)
    c: Vertical(g2)
    c: Distance(g2) = 3
    c: Coincident(g3,g1)
    c: Horizontal(g3)
    c: Distance(g3) = 3
    c: Coincident(g4,g2)
    c: Horizontal(g4)
    c: Distance(g4) = 3
    c: Vertical(g5)
    c: Vertical(g6)
    c: Coincident(g7,g6)
    c: Coincident(g7,g5)
    c: Weight(g8) = 1
    c: Equal(g8,g9)
    c: Equal(g8,g10)
    c: Coincident(g11,g4)
    c: InternalAlignment(g8,g11)
    c: InternalAlignment(g9,g11)
    c: InternalAlignment(g10,g11)
    c: InternalAlignment(g12,g11)
    c: InternalAlignment(g13,g11)
    c: Coincident(g17,g5)
    c: Weight(g14) = 1
    c: Equal(g14,g15)
    c: Equal(g14,g16)
    c: Coincident(g17,g3)
    c: InternalAlignment(g14,g17)
    c: InternalAlignment(g15,g17)
    c: InternalAlignment(g16,g17)
    c: InternalAlignment(g18,g17)
    c: InternalAlignment(g19,g17)
    c: Block(g7)
    c: Block(g17)
    c: Block(g11)
    c: Block(g6)
FEATURE [Part::Extrusion] Extrude003
  Base = -> Sketch002
  Dir = (0,0,1)
  DirMode = 2
  FaceMakerClass = Part::FaceMakerBullseye
  LengthFwd = 260
  LengthRev = 0
  Solid = true
  Symmetric = false
FEATURE [Part::Extrusion] Extrude
  Base = -> Sketch
  Dir = (0,0,1)
  DirMode = 2
  FaceMakerClass = Part::FaceMakerBullseye
  LengthFwd = 14
  LengthRev = 0
  Solid = true
  Symmetric = false
